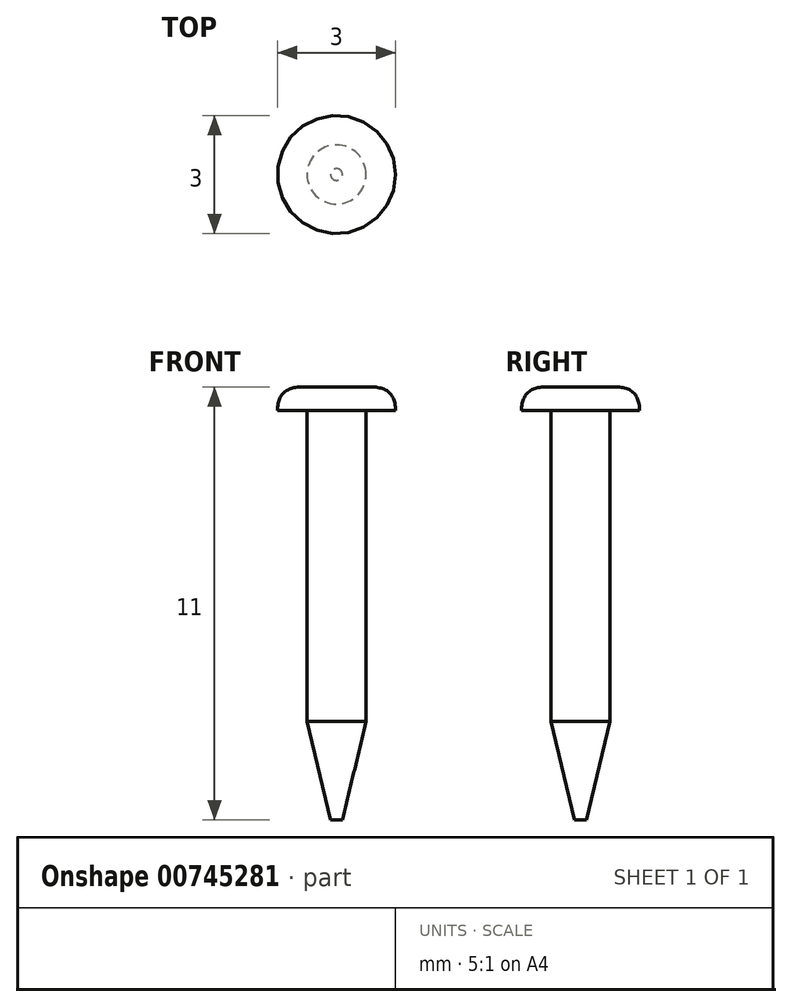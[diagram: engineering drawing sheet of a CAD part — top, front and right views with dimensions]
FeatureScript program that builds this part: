
annotation { "Feature Type Name" : "Feature", "Feature Type Description" : "" }
export const myFeature = defineFeature(function(context is Context, id is Id, definition is map)
    precondition{}
    {
        {
            var Q0;
            Q0=qCreatedBy(makeId("Top.planeOp"),FACE);
            var sketch = newSketch(context, id + "F0", { "sketchPlane" : qUnion([Q0])});
            skCircle(sketch, "E0", {"center": v(0, 0) * mm, "radius": 0.75 * mm});
            skCircle(sketch, "E1", {"center": v(0, 0) * mm, "radius": 1.5 * mm});
            skSolve(sketch);
        }
        {
            var Q0;
            Q0=makeQuery(id+"F0.imprint","IMPRINT",FACE,{"disambiguationData":[TD([[makeQuery(id+"F0.imprint","IMPRINT",EDGE,{"derivedFrom":sQuery(id+"F0.wireOp",EDGE,"E0")}),1.0]])]});
            extrude(context, id + "F1", {"entities" : qUnion([Q0]), "oppositeDirection" : true, "depth" : 10.4 * mm, "offsetDistance" : 25 * mm});
        }
        {
            var Q0;
            Q0 = qSketchRegion(id + "F0", true);
            var Q1;
            Q1=makeQuery(id+"F1.opExtrude","CAP_FACE",FACE,{"disambiguationData":[OSD([sQuery(id+"F0.wireOp",EDGE,"E0")])],"isStart":true});
            extrude(context, id + "F2", {"entities" : qUnion([Q0, Q1]), "operationType" : NewBodyOperationType.ADD, "depth" : 0.6 * mm, "offsetDistance" : 25 * mm});
        }
        {
            var Q0;
            Q0=makeQuery(id+"F1.opExtrude","CAP_EDGE",EDGE,{"disambiguationData":[OSD([sQuery(id+"F0.wireOp",EDGE,"E0")])],"isStart":false});
            chamfer(context, id + "F3", {"entities" : qUnion([Q0]), "chamferType" : ChamferType.TWO_OFFSETS, "width1" : 2.5 * mm, "oppositeDirection" : false, "width2" : 0.6 * mm, "tangentPropagation" : true});
        }
        {
            var Q0;
            Q0=makeQuery(id+"F2.opExtrude","CAP_EDGE",EDGE,{"disambiguationData":[OSD([sQuery(id+"F0.wireOp",EDGE,"E1")])],"isStart":false});
            fillet(context, id + "F4", {"entities" : qUnion([Q0]), "radius" : 0.6 * mm, "rho" : 0.5, "crossSection" : FilletCrossSection.CONIC, "allowEdgeOverflow" : false});
        }
    });
